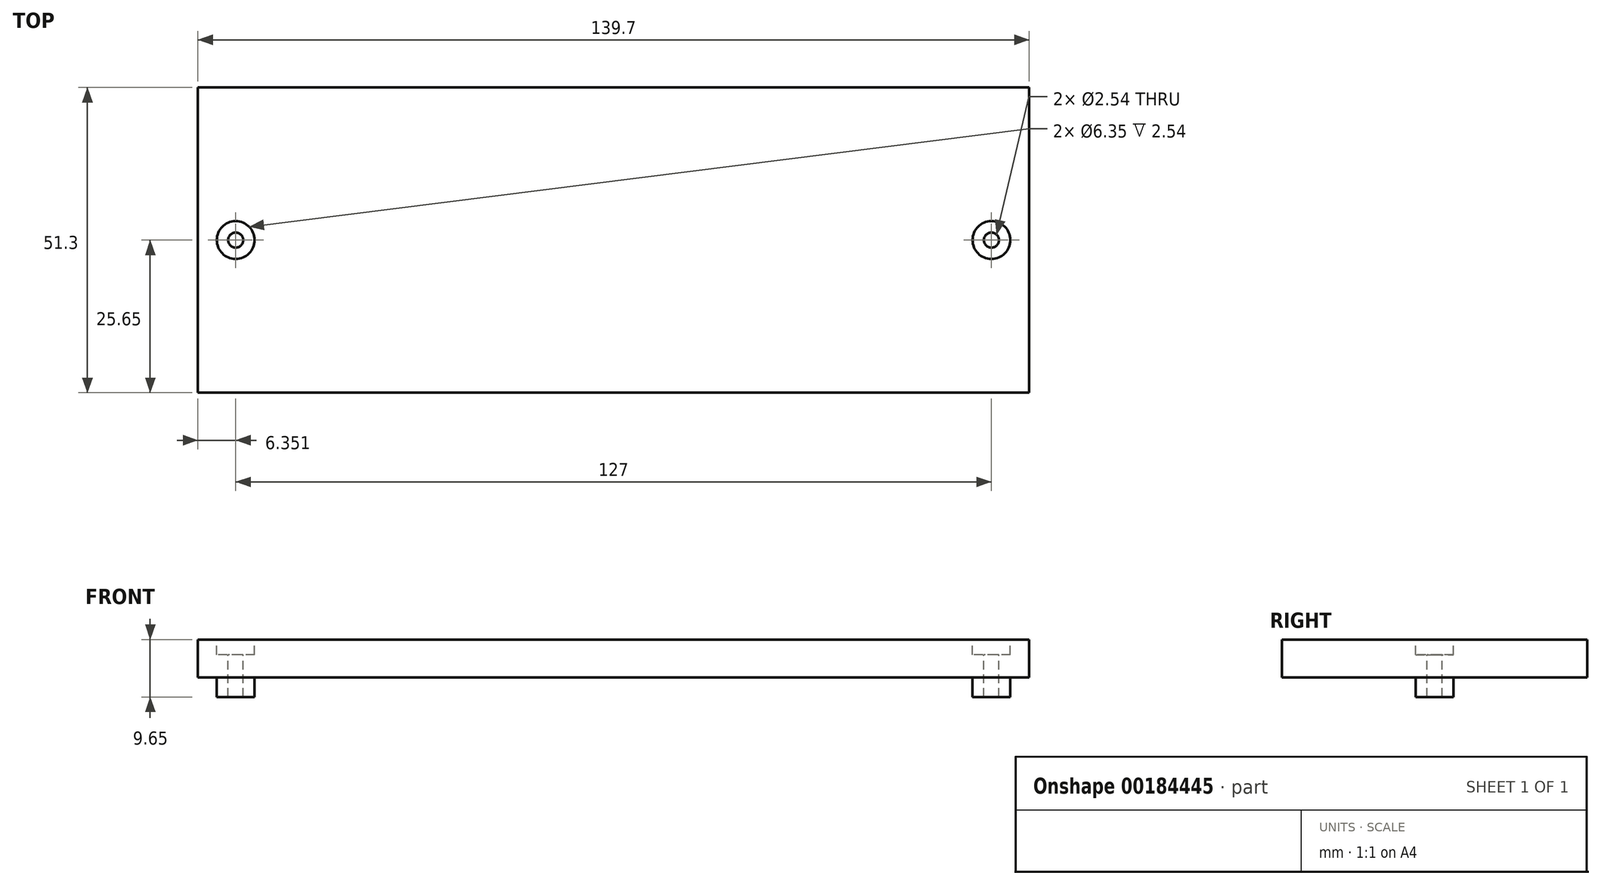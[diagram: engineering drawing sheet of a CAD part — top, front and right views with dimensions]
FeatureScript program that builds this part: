
annotation { "Feature Type Name" : "Feature", "Feature Type Description" : "" }
export const myFeature = defineFeature(function(context is Context, id is Id, definition is map)
    precondition{}
    {
        {
            var Q0;
            Q0=qCreatedBy(makeId("Top.planeOp"),FACE);
            var sketch = newSketch(context, id + "F0", { "sketchPlane" : qUnion([Q0])});
            skLineSegment(sketch, "E0.bottom", {"start": v(-51.48, 31.25) * mm, "end": v(88.22, 31.25) * mm});
            skLineSegment(sketch, "E0.top", {"start": v(-51.48, -20.05) * mm, "end": v(88.22, -20.05) * mm});
            skLineSegment(sketch, "E0.left", {"start": v(-51.48, 31.25) * mm, "end": v(-51.48, -20.05) * mm});
            skLineSegment(sketch, "E0.right", {"start": v(88.22, 31.25) * mm, "end": v(88.22, -20.05) * mm});
            skSolve(sketch);
        }
        {
            var Q0;
            Q0=makeQuery(id+"F0.imprint","IMPRINT",FACE,{"disambiguationData":[TD([[makeQuery(id+"F0.imprint","IMPRINT",EDGE,{"derivedFrom":sQuery(id+"F0.wireOp",EDGE,"E0.bottom")}),-1.0]])]});
            extrude(context, id + "F1", {"entities" : qUnion([Q0]), "depth" : 6.35 * mm});
        }
        {
            var Q0;
            Q0=makeQuery(id+"F1.opExtrude","CAP_FACE",FACE,{"disambiguationData":[OSD([sQuery(id+"F0.wireOp",EDGE,"E0.bottom"),sQuery(id+"F0.wireOp",EDGE,"E0.top"),sQuery(id+"F0.wireOp",EDGE,"E0.left"),sQuery(id+"F0.wireOp",EDGE,"E0.right")])],"isStart":false});
            var sketch = newSketch(context, id + "F2", { "sketchPlane" : qUnion([Q0])});
            skLineSegment(sketch, "E1", {"start": v(-51.48, 5.6) * mm, "end": v(-45.13, 5.6) * mm});
            skLineSegment(sketch, "E2", {"start": v(88.22, 5.6) * mm, "end": v(81.87, 5.6) * mm});
            skPoint(sketch, "E2.endSnap0", {"position": v(88.22, 5.6) * mm});
            skCircle(sketch, "E3", {"center": v(-45.13, 5.6) * mm, "radius": 1.27 * mm});
            skCircle(sketch, "E4", {"center": v(81.87, 5.6) * mm, "radius": 1.27 * mm});
            skCircle(sketch, "E5", {"center": v(-45.13, 5.6) * mm, "radius": 3.18 * mm});
            skCircle(sketch, "E6", {"center": v(81.87, 5.6) * mm, "radius": 3.18 * mm});
            skSolve(sketch);
        }
        {
            var Q0;
            Q0=makeQuery(id+"F2.imprint","IMPRINT",FACE,{"disambiguationData":[TD([[makeQuery(id+"F2.imprint","IMPRINT",EDGE,{"derivedFrom":sQuery(id+"F2.wireOp",EDGE,"E3")}),1.0]])]});
            var Q1;
            Q1=makeQuery(id+"F2.imprint","IMPRINT",FACE,{"disambiguationData":[TD([[makeQuery(id+"F2.imprint","IMPRINT",EDGE,{"derivedFrom":sQuery(id+"F2.wireOp",EDGE,"E4")}),1.0]])]});
            extrude(context, id + "F3", {"entities" : qUnion([Q0, Q1]), "operationType" : NewBodyOperationType.REMOVE, "oppositeDirection" : true, "depth" : 10.4 * mm});
        }
        {
            var Q0;
            Q0=makeQuery(id+"F2.imprint","IMPRINT",FACE,{"disambiguationData":[TD([[makeQuery(id+"F2.imprint","IMPRINT",EDGE,{"derivedFrom":sQuery(id+"F2.wireOp",EDGE,"E3")}),-1.0]])]});
            var Q1;
            Q1=makeQuery(id+"F2.imprint","IMPRINT",FACE,{"disambiguationData":[TD([[makeQuery(id+"F2.imprint","IMPRINT",EDGE,{"derivedFrom":sQuery(id+"F2.wireOp",EDGE,"E4")}),-1.0]])]});
            extrude(context, id + "F4", {"entities" : qUnion([Q0, Q1]), "operationType" : NewBodyOperationType.REMOVE, "oppositeDirection" : true, "depth" : 2.54 * mm});
        }
        {
            var Q0;
            Q0=makeQuery(id+"F4.boolean.opBoolean","COPY",FACE,{"derivedFrom":makeQuery(id+"F4.opExtrude","CAP_FACE",FACE,{"disambiguationData":[OSD([sQuery(id+"F2.wireOp",EDGE,"E3"),sQuery(id+"F2.wireOp",EDGE,"E5")])],"isStart":false})});
            var Q1;
            Q1=makeQuery(id+"F4.boolean.opBoolean","COPY",FACE,{"derivedFrom":makeQuery(id+"F4.opExtrude","CAP_FACE",FACE,{"disambiguationData":[OSD([sQuery(id+"F2.wireOp",EDGE,"E4"),sQuery(id+"F2.wireOp",EDGE,"E6")])],"isStart":false})});
            extrude(context, id + "F5", {"entities" : qUnion([Q0, Q1]), "operationType" : NewBodyOperationType.ADD, "oppositeDirection" : true, "depth" : 7.11 * mm});
        }
    });
